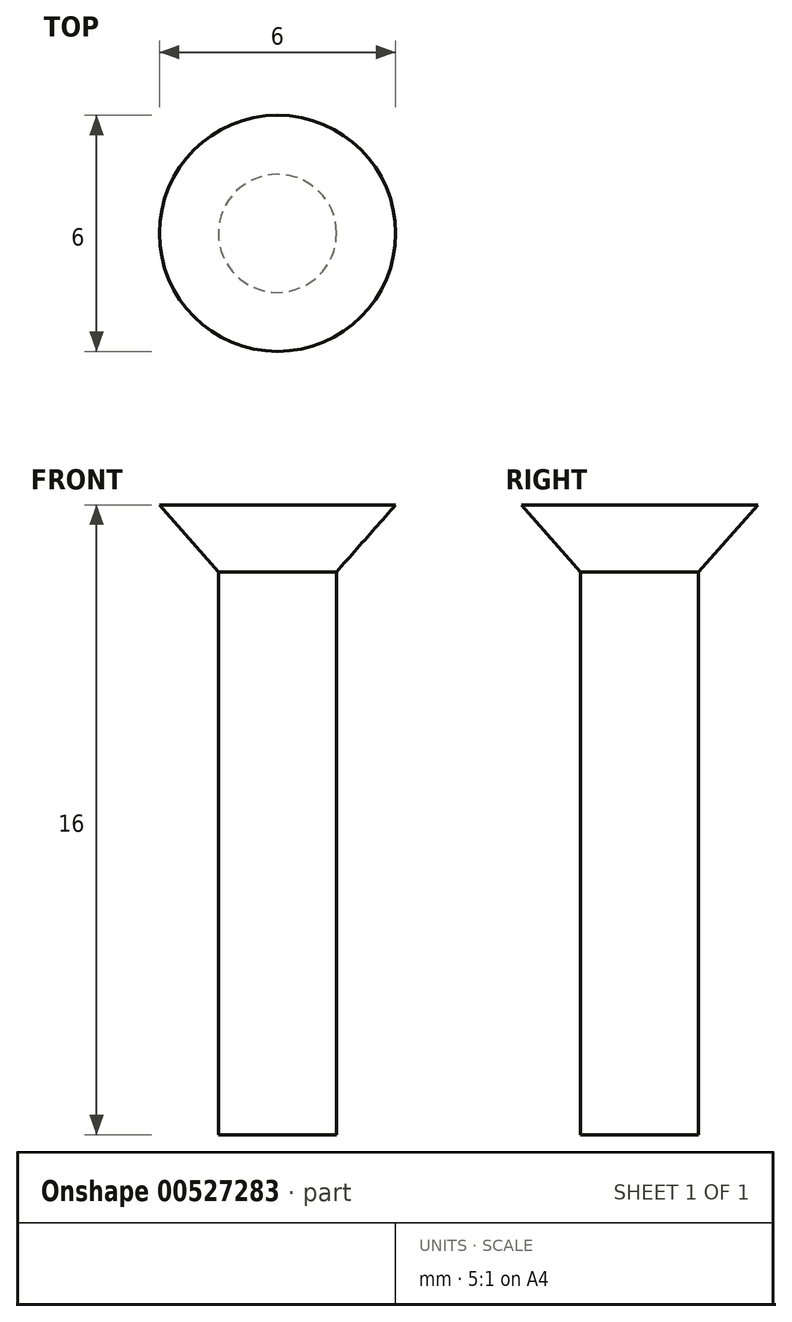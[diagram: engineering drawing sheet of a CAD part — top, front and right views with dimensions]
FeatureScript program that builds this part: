
annotation { "Feature Type Name" : "Feature", "Feature Type Description" : "" }
export const myFeature = defineFeature(function(context is Context, id is Id, definition is map)
    precondition{}
    {
        {
            var Q0;
            Q0=qCreatedBy(makeId("Top.planeOp"),FACE);
            var sketch = newSketch(context, id + "F0", { "sketchPlane" : qUnion([Q0])});
            skCircle(sketch, "E0", {"center": v(0, 0) * mm, "radius": 3 * mm});
            skSolve(sketch);
        }
        {
            var Q0;
            Q0=qCreatedBy(makeId("Top.planeOp"),FACE);
            cPlane(context, id + "F1", {"entities" : qUnion([Q0]), "cplaneType" : CPlaneType.OFFSET, "offset" : 1.7 * mm, "oppositeDirection" : true, "width" : 150 * mm, "height" : 150 * mm});
        }
        {
            var Q0;
            Q0=qCreatedBy(id+"F1.planeOp",FACE);
            var sketch = newSketch(context, id + "F2", { "sketchPlane" : qUnion([Q0])});
            skCircle(sketch, "E1", {"center": v(0, 0) * mm, "radius": 1.5 * mm});
            skSolve(sketch);
        }
        {
            var Q0;
            Q0=makeQuery(id+"F0.imprint","IMPRINT",FACE,{"disambiguationData":[TD([[makeQuery(id+"F0.imprint","IMPRINT",EDGE,{"derivedFrom":sQuery(id+"F0.wireOp",EDGE,"E0")}),1.0]])]});
            var Q1;
            Q1=makeQuery(id+"F2.imprint","IMPRINT",FACE,{"disambiguationData":[TD([[makeQuery(id+"F2.imprint","IMPRINT",EDGE,{"derivedFrom":sQuery(id+"F2.wireOp",EDGE,"E1")}),1.0]])]});
            loft(context, id + "F3", {"sheetProfilesArray" : [{ "sheetProfileEntities" : qUnion([Q0]) }, { "sheetProfileEntities" : qUnion([Q1]) }]});
        }
        {
            var Q0;
            Q0=makeQuery(id+"F3.opLoft","CAP_FACE",FACE,{"disambiguationData":[OSD([makeQuery(id+"F2.imprint","IMPRINT",FACE,{"disambiguationData":[TD([[makeQuery(id+"F2.imprint","IMPRINT",EDGE,{"derivedFrom":sQuery(id+"F2.wireOp",EDGE,"E1")}),1.0]])]})])],"isStart":true});
            extrude(context, id + "F4", {"entities" : qUnion([Q0]), "operationType" : NewBodyOperationType.ADD, "depth" : 14.3 * mm, "offsetDistance" : 25 * mm});
        }
    });
